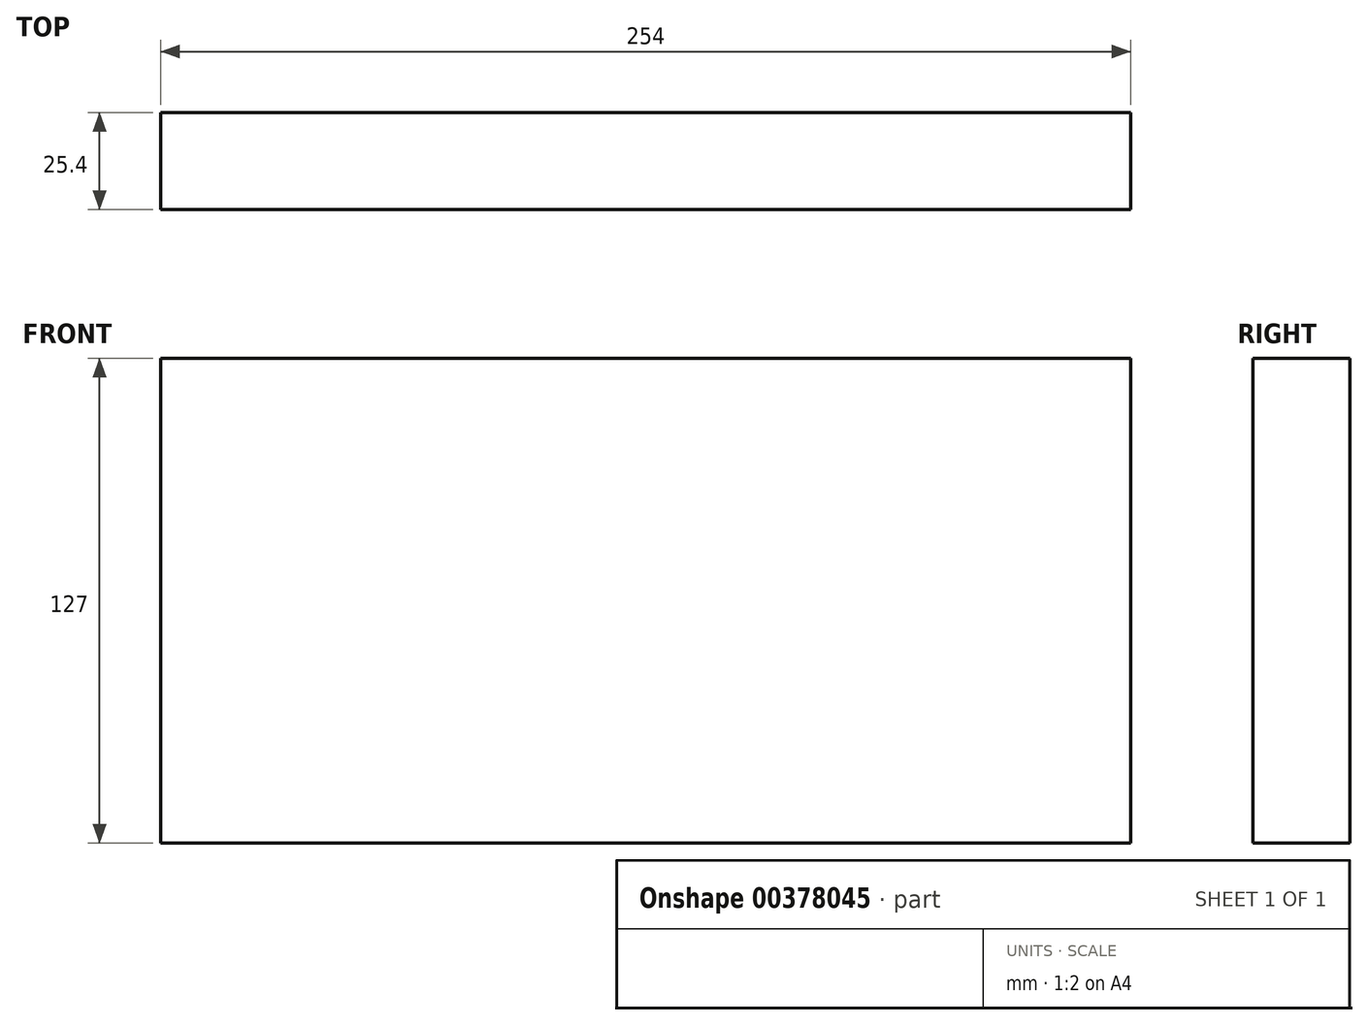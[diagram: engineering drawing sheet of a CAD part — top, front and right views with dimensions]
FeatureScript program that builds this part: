
annotation { "Feature Type Name" : "Feature", "Feature Type Description" : "" }
export const myFeature = defineFeature(function(context is Context, id is Id, definition is map)
    precondition{}
    {
        {
            var Q0;
            Q0=qCreatedBy(makeId("Front.planeOp"),FACE);
            var sketch = newSketch(context, id + "F0", { "sketchPlane" : qUnion([Q0])});
            skLineSegment(sketch, "E0.bottom", {"start": v(-126.5, 51.26) * mm, "end": v(127.5, 51.26) * mm});
            skLineSegment(sketch, "E0.top", {"start": v(-126.5, -75.74) * mm, "end": v(127.5, -75.74) * mm});
            skLineSegment(sketch, "E0.left", {"start": v(-126.5, 51.26) * mm, "end": v(-126.5, -75.74) * mm});
            skLineSegment(sketch, "E0.right", {"start": v(127.5, 51.26) * mm, "end": v(127.5, -75.74) * mm});
            skLineSegment(sketch, "E1.left", {"start": v(-126.5, 51.26) * mm, "end": v(-126.5, 51.26) * mm});
            skLineSegment(sketch, "E1.right", {"start": v(127.5, 51.26) * mm, "end": v(127.5, 51.26) * mm});
            skSolve(sketch);
        }
        {
            var Q0;
            Q0=makeQuery(id+"F0.imprint","IMPRINT",FACE,{"disambiguationData":[TD([[makeQuery(id+"F0.imprint","IMPRINT",EDGE,{"derivedFrom":sQuery(id+"F0.wireOp",EDGE,"E0.top")}),1.0]])]});
            extrude(context, id + "F1", {"entities" : qUnion([Q0]), "depth" : 25.4 * mm});
        }
    });
